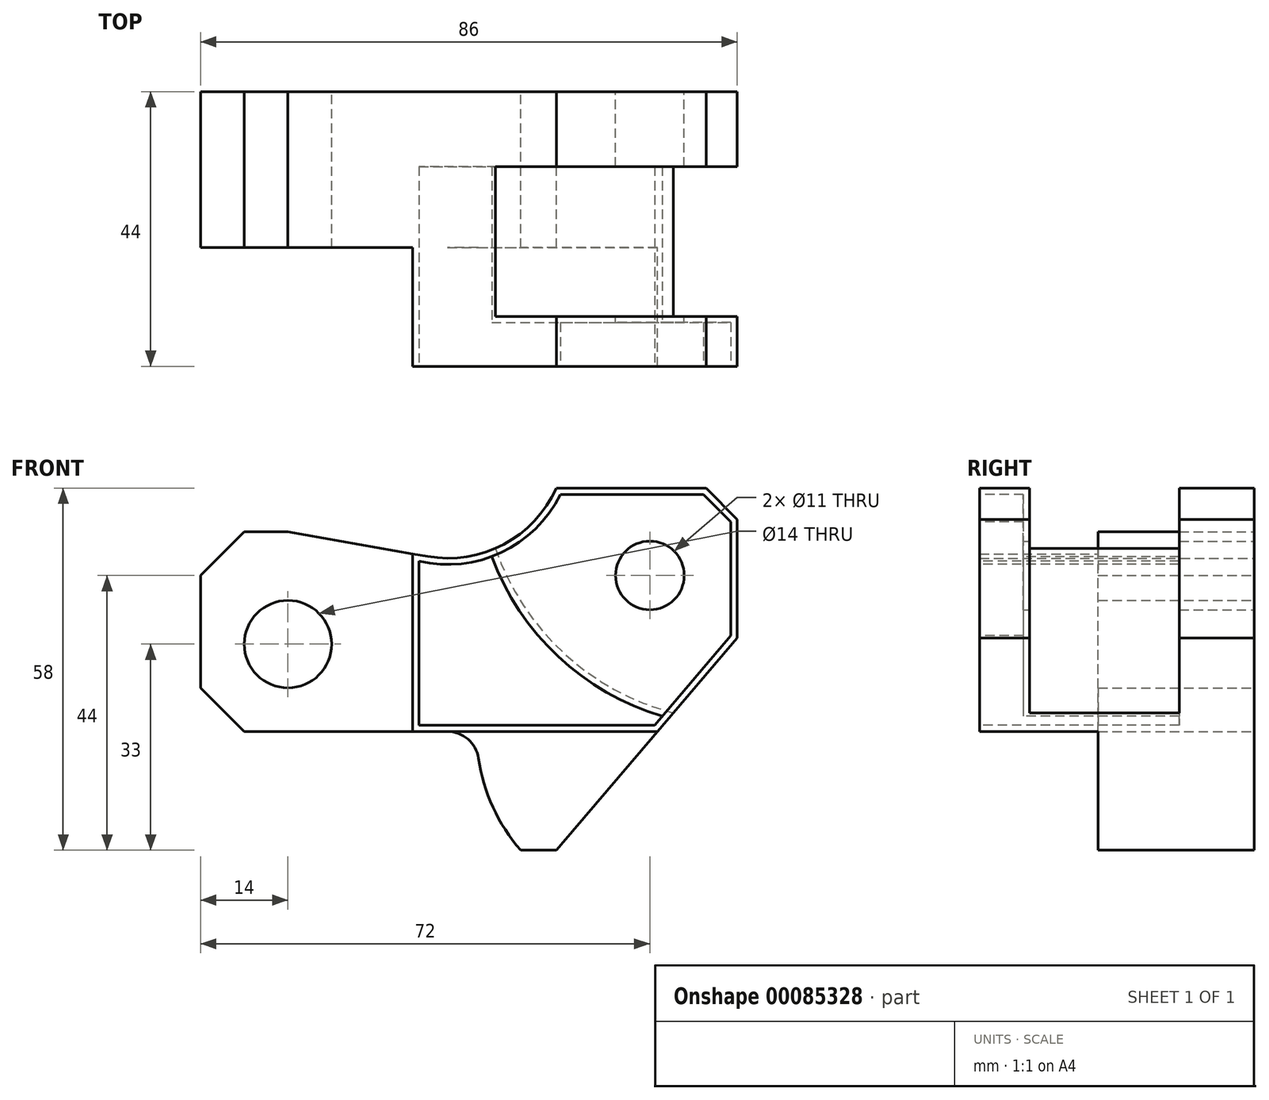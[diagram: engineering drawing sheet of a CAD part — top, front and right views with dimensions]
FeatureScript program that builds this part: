
annotation { "Feature Type Name" : "Feature", "Feature Type Description" : "" }
export const myFeature = defineFeature(function(context is Context, id is Id, definition is map)
    precondition{}
    {
        {
            var Q0;
            Q0=qCreatedBy(makeId("Front.planeOp"),FACE);
            var sketch = newSketch(context, id + "F0", { "sketchPlane" : qUnion([Q0])});
            skLineSegment(sketch, "E0", {"start": v(-29, 24) * mm, "end": v(-5, 24) * mm});
            skLineSegment(sketch, "E1", {"start": v(-5, 24) * mm, "end": v(0, 19) * mm});
            skLineSegment(sketch, "E2", {"start": v(0, 19) * mm, "end": v(0, 0) * mm});
            skLineSegment(sketch, "E3", {"start": v(0, 0) * mm, "end": v(-29, -34) * mm});
            skLineSegment(sketch, "E4", {"start": v(-29, -34) * mm, "end": v(-34.7, -34) * mm});
            skLineSegment(sketch, "E5", {"start": v(-49.64, 13.06) * mm, "end": v(-72, 17) * mm});
            skLineSegment(sketch, "E6", {"start": v(-72, 17) * mm, "end": v(-79, 17) * mm});
            skLineSegment(sketch, "E7", {"start": v(-79, 17) * mm, "end": v(-86, 10) * mm});
            skLineSegment(sketch, "E8", {"start": v(-86, 10) * mm, "end": v(-86, -8) * mm});
            skLineSegment(sketch, "E9", {"start": v(-86, -8) * mm, "end": v(-79, -15) * mm});
            skLineSegment(sketch, "E10", {"start": v(-79, -15) * mm, "end": v(-46.42, -15) * mm});
            skArc(sketch, "E11", {"start": v(-49.64, 13.06) * mm, "mid": v(-37.44, 14.98) * mm, "end": v(-29, 24) * mm});
            skCircle(sketch, "E12", {"center": v(-72, -1) * mm, "radius": 7 * mm});
            skArc(sketch, "E13", {"start": v(-46.42, -15) * mm, "mid": v(-43.16, -16.21) * mm, "end": v(-41.48, -19.26) * mm});
            skArc(sketch, "E14", {"start": v(-41.48, -19.26) * mm, "mid": v(-39.14, -27.12) * mm, "end": v(-34.7, -34) * mm});
            skCircle(sketch, "E15", {"center": v(-14, 10) * mm, "radius": 5.5 * mm});
            skSolve(sketch);
        }
        {
            var Q0;
            Q0=makeQuery(id+"F0.imprint","IMPRINT",FACE,{"disambiguationData":[TD([[makeQuery(id+"F0.imprint","IMPRINT",EDGE,{"derivedFrom":sQuery(id+"F0.wireOp",EDGE,"E0")}),-1.0]])]});
            extrude(context, id + "F1", {"entities" : qUnion([Q0]), "depth" : 44 * mm});
        }
        {
            var Q0;
            Q0=makeQuery(id+"F1.opExtrude","SWEPT_FACE",FACE,{"disambiguationData":[OSD([sQuery(id+"F0.wireOp",EDGE,"E6")])]});
            var sketch = newSketch(context, id + "F2", { "sketchPlane" : qUnion([Q0])});
            skLineSegment(sketch, "E16.0", {"start": v(-49.64, -44) * mm, "end": v(-72, -44) * mm});
            skLineSegment(sketch, "E16.1", {"start": v(-72, -44) * mm, "end": v(-79, -44) * mm});
            skLineSegment(sketch, "E16.2", {"start": v(-79, -44) * mm, "end": v(-86, -44) * mm});
            skLineSegment(sketch, "E16.3", {"start": v(-49.64, -44) * mm, "end": v(-29, -44) * mm});
            skLineSegment(sketch, "E16.4", {"start": v(-29, -44) * mm, "end": v(-5, -44) * mm});
            skLineSegment(sketch, "E16.5", {"start": v(-5, -44) * mm, "end": v(0, -44) * mm});
            skLineSegment(sketch, "E17", {"start": v(-86, -44) * mm, "end": v(-86, -25) * mm});
            skLineSegment(sketch, "E18", {"start": v(-86, -25) * mm, "end": v(-52, -25) * mm});
            skLineSegment(sketch, "E19", {"start": v(-52, -25) * mm, "end": v(-52, -44) * mm});
            skSolve(sketch);
        }
        {
            var Q0;
            {var subQ3=sQuery(id+"F2.wireOp",EDGE,"E19");Q0=makeQuery(id+"F2.imprint","IMPRINT",FACE,{"disambiguationData":[TD([[makeQuery(id+"F2.imprint","IMPRINT",EDGE,{"derivedFrom":subQ3}),-1.0]])]});}
            var Q1;
            {var subQ0=sQuery(id+"F2.wireOp",EDGE,"E16.1");Q1=makeQuery(id+"F2.imprint","IMPRINT",FACE,{"disambiguationData":[TD([[makeQuery(id+"F2.imprint","IMPRINT",EDGE,{"derivedFrom":subQ0}),-1.0]])]});}
            var Q2;
            {var subQ0=sQuery(id+"F2.wireOp",EDGE,"E16.2");Q2=makeQuery(id+"F2.imprint","IMPRINT",FACE,{"disambiguationData":[TD([[makeQuery(id+"F2.imprint","IMPRINT",EDGE,{"derivedFrom":subQ0}),-1.0]])]});}
            extrude(context, id + "F3", {"entities" : qUnion([Q0, Q1, Q2]), "operationType" : NewBodyOperationType.REMOVE, "endBound" : BoundingType.THROUGH_ALL, "oppositeDirection" : true, "depth" : 25 * mm});
        }
        {
            var Q0;
            Q0=qCreatedBy(makeId("Front.planeOp"),FACE);
            cPlane(context, id + "F4", {"entities" : qUnion([Q0]), "cplaneType" : CPlaneType.OFFSET, "offset" : 12 * mm, "width" : 150 * mm, "height" : 150 * mm});
        }
        {
            var Q0;
            Q0=qCreatedBy(id+"F4.planeOp",FACE);
            var sketch = newSketch(context, id + "F5", { "sketchPlane" : qUnion([Q0])});
            skLineSegment(sketch, "E20.0", {"start": v(0, 0) * mm, "end": v(-29, -34) * mm});
            skArc(sketch, "E20.1", {"start": v(-49.64, 13.06) * mm, "mid": v(-37.44, 14.98) * mm, "end": v(-29, 24) * mm});
            skLineSegment(sketch, "E20.2", {"start": v(-29, 24) * mm, "end": v(-5, 24) * mm});
            skLineSegment(sketch, "E21.0", {"start": v(-5, 24) * mm, "end": v(0, 19) * mm});
            skLineSegment(sketch, "E21.1.0", {"start": v(-52, 13.47) * mm, "end": v(-52, -15) * mm});
            skLineSegment(sketch, "E21.1.5", {"start": v(-29, -34) * mm, "end": v(0, 0) * mm});
            skLineSegment(sketch, "E21.1.6", {"start": v(0, 0) * mm, "end": v(0, 19) * mm});
            skLineSegment(sketch, "E21.1.7", {"start": v(0, 19) * mm, "end": v(-5, 24) * mm});
            skLineSegment(sketch, "E21.1.8", {"start": v(-5, 24) * mm, "end": v(-29, 24) * mm});
            skArc(sketch, "E21.1.9", {"start": v(-29, 24) * mm, "mid": v(-37.44, 14.98) * mm, "end": v(-49.64, 13.06) * mm});
            skLineSegment(sketch, "E21.1.10", {"start": v(-49.64, 13.06) * mm, "end": v(-52, 13.47) * mm});
            skLineSegment(sketch, "E21.2", {"start": v(0, 19) * mm, "end": v(0, 0) * mm});
            skArc(sketch, "E22", {"start": v(-38.76, 14.34) * mm, "mid": v(-27.82, -2.42) * mm, "end": v(-10.24, -12) * mm});
            skSolve(sketch);
        }
        {
            var Q0;
            Q0 = qSketchRegion(id + "F5", true);
            extrude(context, id + "F6", {"entities" : qUnion([Q0]), "operationType" : NewBodyOperationType.REMOVE, "depth" : 24 * mm});
        }
        {
            var Q0;
            Q0=makeQuery(id+"F1.opExtrude","CAP_FACE",FACE,{"disambiguationData":[OSD([sQuery(id+"F0.wireOp",EDGE,"E0"),sQuery(id+"F0.wireOp",EDGE,"E1"),sQuery(id+"F0.wireOp",EDGE,"E2"),sQuery(id+"F0.wireOp",EDGE,"E3"),sQuery(id+"F0.wireOp",EDGE,"E4"),sQuery(id+"F0.wireOp",EDGE,"E5"),sQuery(id+"F0.wireOp",EDGE,"E6"),sQuery(id+"F0.wireOp",EDGE,"E7"),sQuery(id+"F0.wireOp",EDGE,"E8"),sQuery(id+"F0.wireOp",EDGE,"E9"),sQuery(id+"F0.wireOp",EDGE,"E10"),sQuery(id+"F0.wireOp",EDGE,"E11"),sQuery(id+"F0.wireOp",EDGE,"E12"),sQuery(id+"F0.wireOp",EDGE,"E13"),sQuery(id+"F0.wireOp",EDGE,"E14"),sQuery(id+"F0.wireOp",EDGE,"E15")])],"isStart":false});
            var sketch = newSketch(context, id + "F7", { "sketchPlane" : qUnion([Q0])});
            skLineSegment(sketch, "E23.0", {"start": v(-52, -15) * mm, "end": v(-46.42, -15) * mm});
            skLineSegment(sketch, "E24", {"start": v(-52, -15) * mm, "end": v(24.73, -15) * mm});
            skPoint(sketch, "E24.endSnap0", {"position": v(-49.21, -15) * mm});
            skLineSegment(sketch, "E25", {"start": v(24.73, -15) * mm, "end": v(24.73, -51.12) * mm});
            skLineSegment(sketch, "E26", {"start": v(24.73, -51.12) * mm, "end": v(-52, -51.12) * mm});
            skLineSegment(sketch, "E27", {"start": v(-52, -51.12) * mm, "end": v(-52, -15) * mm});
            skSolve(sketch);
        }
        {
            var Q0;
            {var subQ0=sQuery(id+"F7.wireOp",EDGE,"E25");Q0=makeQuery(id+"F7.imprint","IMPRINT",FACE,{"disambiguationData":[TD([[makeQuery(id+"F7.imprint","IMPRINT",EDGE,{"derivedFrom":subQ0}),-1.0]])]});}
            var Q1;
            {var subQ1=makeQuery(id+"F1.opExtrude","CAP_EDGE",EDGE,{"disambiguationData":[OSD([sQuery(id+"F0.wireOp",EDGE,"E4")])],"isStart":false});Q1=makeQuery(id+"F7.imprint","IMPRINT",FACE,{"disambiguationData":[TD([[makeQuery(id+"F7.imprint","IMPRINT",EDGE,{"derivedFrom":subQ1}),-1.0]])]});}
            extrude(context, id + "F8", {"entities" : qUnion([Q0, Q1]), "operationType" : NewBodyOperationType.REMOVE, "oppositeDirection" : true, "depth" : 19 * mm});
        }
        {
            var Q0;
            Q0=makeQuery(id+"F1.opExtrude","CAP_FACE",FACE,{"disambiguationData":[OSD([sQuery(id+"F0.wireOp",EDGE,"E0"),sQuery(id+"F0.wireOp",EDGE,"E1"),sQuery(id+"F0.wireOp",EDGE,"E2"),sQuery(id+"F0.wireOp",EDGE,"E3"),sQuery(id+"F0.wireOp",EDGE,"E4"),sQuery(id+"F0.wireOp",EDGE,"E5"),sQuery(id+"F0.wireOp",EDGE,"E6"),sQuery(id+"F0.wireOp",EDGE,"E7"),sQuery(id+"F0.wireOp",EDGE,"E8"),sQuery(id+"F0.wireOp",EDGE,"E9"),sQuery(id+"F0.wireOp",EDGE,"E10"),sQuery(id+"F0.wireOp",EDGE,"E11"),sQuery(id+"F0.wireOp",EDGE,"E12"),sQuery(id+"F0.wireOp",EDGE,"E13"),sQuery(id+"F0.wireOp",EDGE,"E14"),sQuery(id+"F0.wireOp",EDGE,"E15")])],"isStart":false});
            var sketch = newSketch(context, id + "F9", { "sketchPlane" : qUnion([Q0])});
            skLineSegment(sketch, "E28.0", {"start": v(-51, -14) * mm, "end": v(-51, 12.32) * mm});
            skLineSegment(sketch, "E28.1", {"start": v(-51, -14) * mm, "end": v(-13.26, -14) * mm});
            skLineSegment(sketch, "E28.2", {"start": v(-28.36, 23) * mm, "end": v(-5.41, 23) * mm});
            skLineSegment(sketch, "E28.3", {"start": v(-5.41, 23) * mm, "end": v(-1, 18.59) * mm});
            skLineSegment(sketch, "E28.4", {"start": v(-1, 18.59) * mm, "end": v(-1, 0.37) * mm});
            skArc(sketch, "E28.5", {"start": v(-51, 12.32) * mm, "mid": v(-37.8, 13.68) * mm, "end": v(-28.36, 23) * mm});
            skLineSegment(sketch, "E28.6", {"start": v(-1, 0.37) * mm, "end": v(-13.26, -14) * mm});
            skArc(sketch, "E29.0", {"start": v(-39.35, 13.03) * mm, "mid": v(-28.69, -2.97) * mm, "end": v(-12.01, -12.54) * mm});
            skSolve(sketch);
        }
        {
            var Q0;
            {var subQ1=sQuery(id+"F9.wireOp",EDGE,"E28.2");Q0=makeQuery(id+"F9.imprint","IMPRINT",FACE,{"disambiguationData":[TD([[makeQuery(id+"F9.imprint","IMPRINT",EDGE,{"derivedFrom":subQ1}),-1.0]])]});}
            extrude(context, id + "F10", {"entities" : qUnion([Q0]), "operationType" : NewBodyOperationType.REMOVE, "oppositeDirection" : true, "depth" : 7 * mm});
        }
        {
            var Q0;
            {var subQ4=sQuery(id+"F9.wireOp",EDGE,"E28.0");Q0=makeQuery(id+"F9.imprint","IMPRINT",FACE,{"disambiguationData":[TD([[makeQuery(id+"F9.imprint","IMPRINT",EDGE,{"derivedFrom":subQ4}),-1.0]])]});}
            var Q1;
            Q1=makeQuery(id+"F6.boolean.opBoolean","COPY",FACE,{"derivedFrom":makeQuery(id+"F6.opExtrude","CAP_FACE",FACE,{"disambiguationData":[OSD([sQuery(id+"F5.wireOp",EDGE,"E21.1.5"),sQuery(id+"F5.wireOp",EDGE,"E21.1.7"),sQuery(id+"F5.wireOp",EDGE,"E21.1.8"),sQuery(id+"F5.wireOp",EDGE,"E21.1.9"),sQuery(id+"F5.wireOp",EDGE,"E21.2"),sQuery(id+"F5.wireOp",EDGE,"E22")])],"isStart":true})});
            extrude(context, id + "F11", {"entities" : qUnion([Q0]), "operationType" : NewBodyOperationType.REMOVE, "endBound" : BoundingType.UP_TO_SURFACE, "oppositeDirection" : true, "endBoundEntityFace" : qUnion([Q1]), "depth" : 25 * mm});
        }
    });
